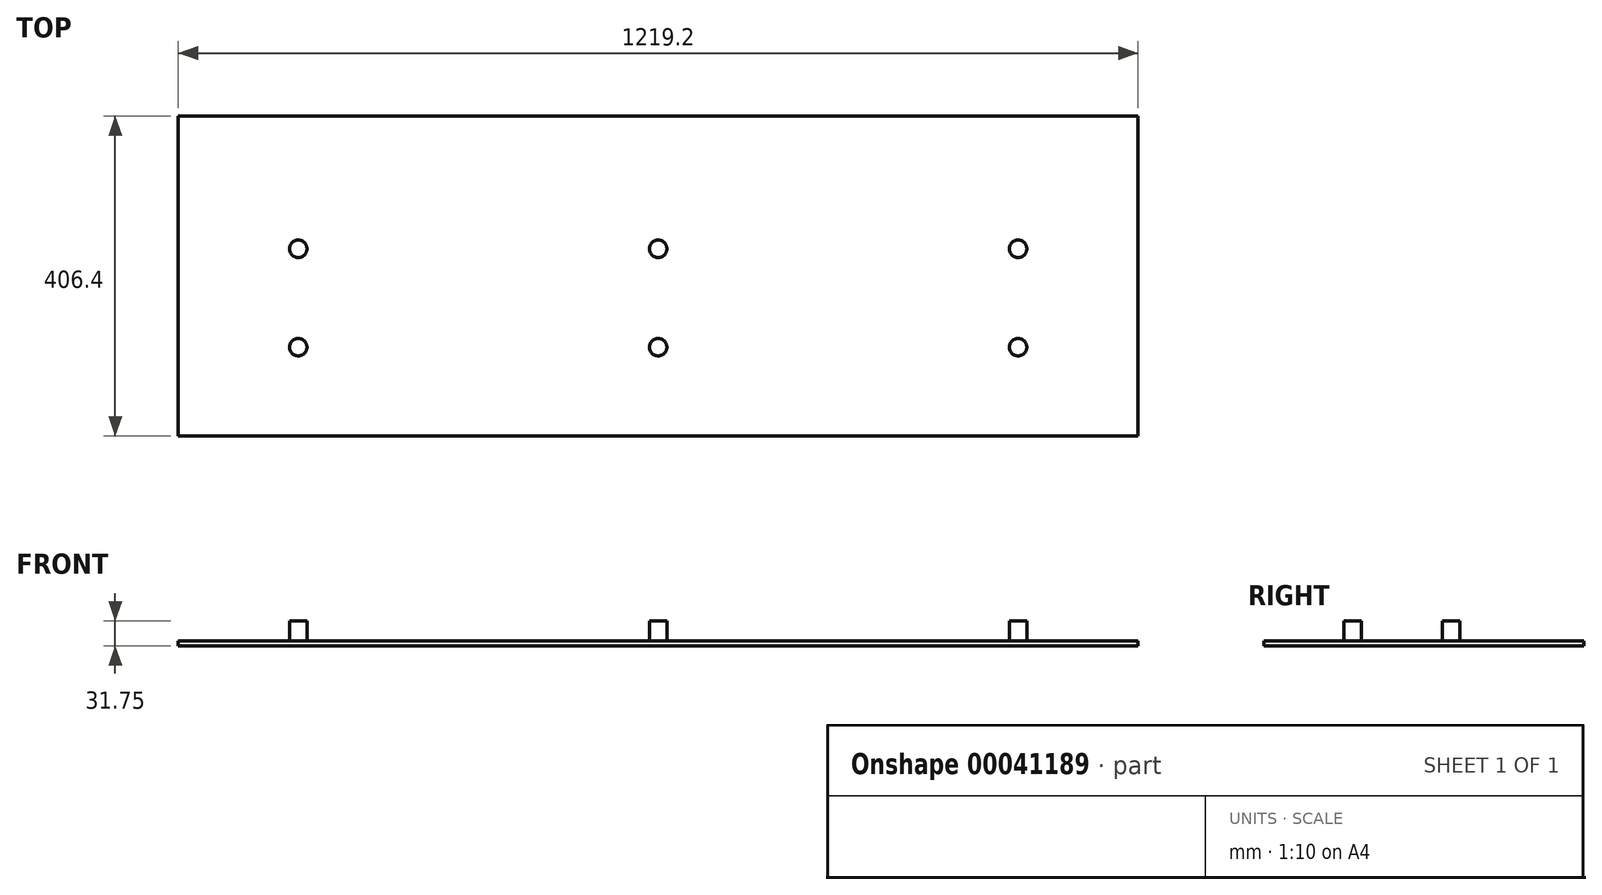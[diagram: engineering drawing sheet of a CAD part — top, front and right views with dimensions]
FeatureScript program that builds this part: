
annotation { "Feature Type Name" : "Feature", "Feature Type Description" : "" }
export const myFeature = defineFeature(function(context is Context, id is Id, definition is map)
    precondition{}
    {
        {
            var Q0;
            Q0=qCreatedBy(makeId("Top.planeOp"),FACE);
            var sketch = newSketch(context, id + "F1", { "sketchPlane" : qUnion([Q0])});
            skLineSegment(sketch, "E0.bottom", {"start": v(0, 406.4) * mm, "end": v(1219.2, 406.4) * mm});
            skLineSegment(sketch, "E0.top", {"start": v(0, 0) * mm, "end": v(1219.2, 0) * mm});
            skLineSegment(sketch, "E0.left", {"start": v(0, 406.4) * mm, "end": v(0, 0) * mm});
            skLineSegment(sketch, "E0.right", {"start": v(1219.2, 406.4) * mm, "end": v(1219.2, 0) * mm});
            skSolve(sketch);
        }
        {
            var Q0;
            Q0=makeQuery(id+"F1.imprint","IMPRINT",FACE,{"disambiguationData":[TD([[makeQuery(id+"F1.imprint","IMPRINT",EDGE,{"derivedFrom":sQuery(id+"F1.wireOp",EDGE,"E0.bottom")}),-1.0]])]});
            extrude(context, id + "F2", {"entities" : qUnion([Q0]), "depth" : 6.35 * mm});
        }
        {
            var Q0;
            Q0=makeQuery(id+"F2.opExtrude","CAP_FACE",FACE,{"disambiguationData":[OSD([sQuery(id+"F1.wireOp",EDGE,"E0.bottom"),sQuery(id+"F1.wireOp",EDGE,"E0.top"),sQuery(id+"F1.wireOp",EDGE,"E0.left"),sQuery(id+"F1.wireOp",EDGE,"E0.right")])],"isStart":false});
            var sketch = newSketch(context, id + "F3", { "sketchPlane" : qUnion([Q0])});
            skCircle(sketch, "E1", {"center": v(152.4, 112.71) * mm, "radius": 11.11 * mm});
            skCircle(sketch, "E2", {"center": v(152.4, 237.71) * mm, "radius": 11.11 * mm});
            skCircle(sketch, "E3.1.0.0", {"center": v(609.6, 237.71) * mm, "radius": 11.11 * mm});
            skCircle(sketch, "E3.1.0.1", {"center": v(609.6, 112.71) * mm, "radius": 11.11 * mm});
            skCircle(sketch, "E3.2.0.0", {"center": v(1066.8, 237.71) * mm, "radius": 11.11 * mm});
            skCircle(sketch, "E3.2.0.1", {"center": v(1066.8, 112.71) * mm, "radius": 11.11 * mm});
            skLineSegment(sketch, "E3.direction1", {"start": v(152.4, 237.71) * mm, "end": v(609.6, 237.71) * mm, "construction": true});
            skSolve(sketch);
        }
        {
            var Q0;
            Q0 = qSketchRegion(id + "F3", true);
            extrude(context, id + "F0", {"entities" : qUnion([Q0]), "operationType" : NewBodyOperationType.ADD, "depth" : 25.4 * mm});
        }
    });
